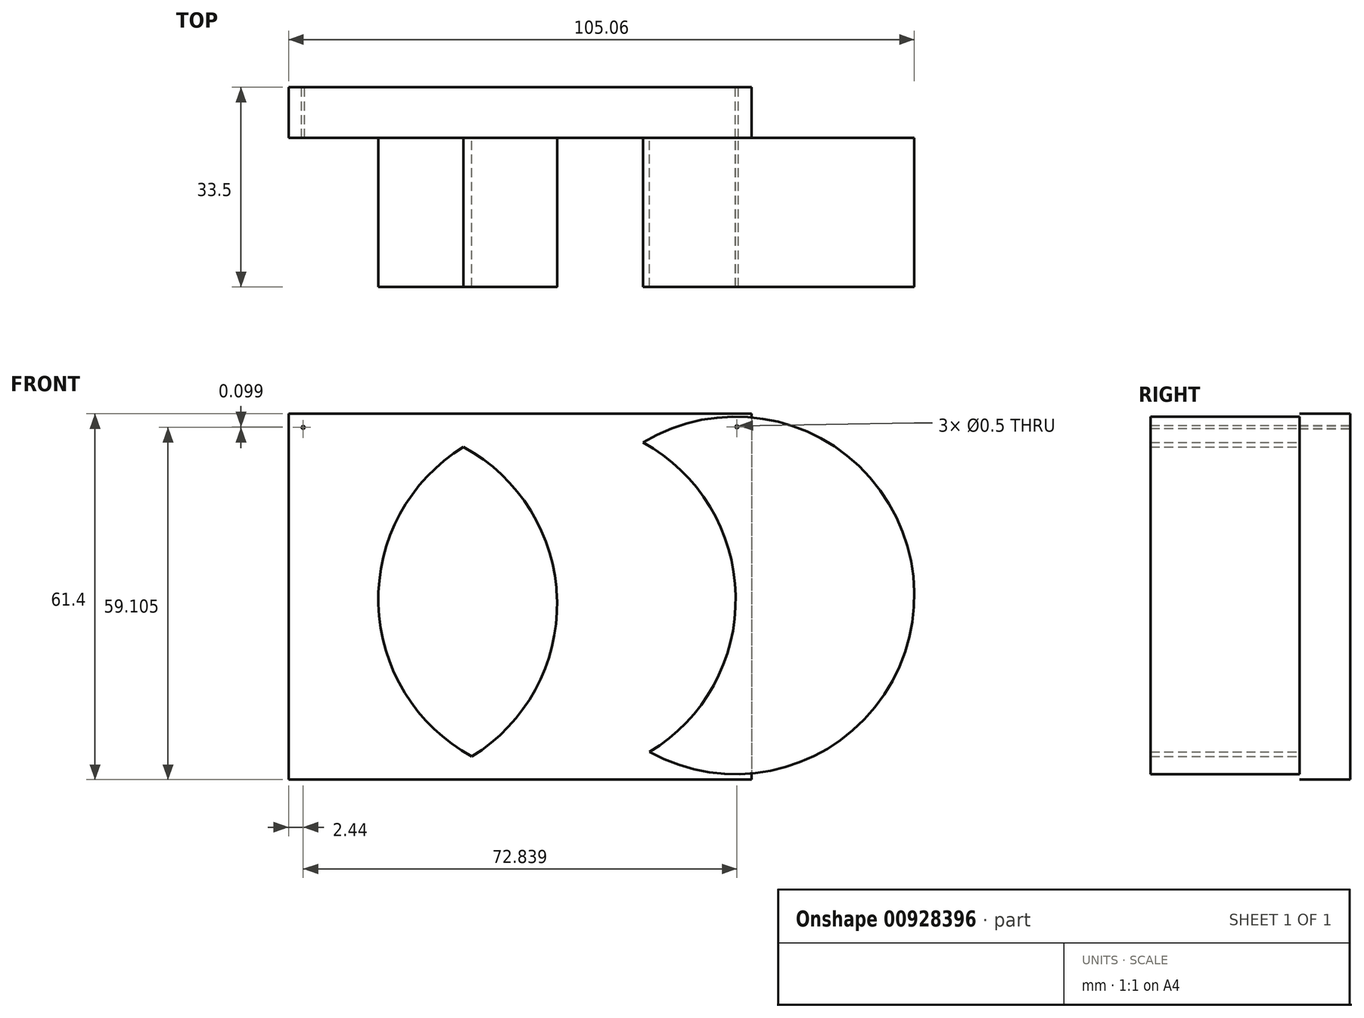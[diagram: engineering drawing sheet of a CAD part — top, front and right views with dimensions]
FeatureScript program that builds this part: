
annotation { "Feature Type Name" : "Feature", "Feature Type Description" : "" }
export const myFeature = defineFeature(function(context is Context, id is Id, definition is map)
    precondition{}
    {
        {
            var Q0;
            Q0=qCreatedBy(makeId("Front.planeOp"),FACE);
            var sketch = newSketch(context, id + "F0", { "sketchPlane" : qUnion([Q0])});
            skCircle(sketch, "E0", {"center": v(-38.91, 38.4) * mm, "radius": 30 * mm});
            skCircle(sketch, "E1", {"center": v(-8.92, 39.21) * mm, "radius": 30 * mm});
            skCircle(sketch, "E2", {"center": v(21.07, 39.84) * mm, "radius": 30 * mm});
            skSolve(sketch);
        }
        {
            var Q0;
            {var subQ0=sQuery(id+"F0.wireOp",EDGE,"E1");var subQ1=sQuery(id+"F0.wireOp",EDGE,"E0");var subQ2=makeQuery(id+"F0.imprint","INTERSECT",VERTEX,{"disambiguationData":[OD(0.0)],"derivedFrom":[subQ1,subQ0]});Q0=makeQuery(id+"F0.imprint","IMPRINT",FACE,{"disambiguationData":[TD([[makeQuery(id+"F0.imprint","IMPRINT",EDGE,{"disambiguationData":[TD([[subQ2,-1.0]])],"derivedFrom":subQ1}),1.0]])]});}
            var Q1;
            {var subQ0=sQuery(id+"F0.wireOp",EDGE,"E2");var subQ1=sQuery(id+"F0.wireOp",EDGE,"E1");var subQ2=makeQuery(id+"F0.imprint","INTERSECT",VERTEX,{"disambiguationData":[OD(0.0)],"derivedFrom":[subQ1,subQ0]});Q1=makeQuery(id+"F0.imprint","IMPRINT",FACE,{"disambiguationData":[TD([[makeQuery(id+"F0.imprint","IMPRINT",EDGE,{"disambiguationData":[TD([[subQ2,1.0]])],"derivedFrom":subQ1}),-1.0]])]});}
            var Q2;
            {var subQ0=sQuery(id+"F0.wireOp",EDGE,"E1");var subQ1=sQuery(id+"F0.wireOp",EDGE,"E0");var subQ2=makeQuery(id+"F0.imprint","INTERSECT",VERTEX,{"disambiguationData":[OD(0.0)],"derivedFrom":[subQ1,subQ0]});Q2=makeQuery(id+"F0.imprint","IMPRINT",FACE,{"disambiguationData":[TD([[makeQuery(id+"F0.imprint","IMPRINT",EDGE,{"disambiguationData":[TD([[subQ2,1.0]])],"derivedFrom":subQ1}),-1.0]])]});}
            var Q3;
            {var subQ0=sQuery(id+"F0.wireOp",EDGE,"E1");var subQ1=sQuery(id+"F0.wireOp",EDGE,"E0");var subQ2=makeQuery(id+"F0.imprint","INTERSECT",VERTEX,{"disambiguationData":[OD(1.0)],"derivedFrom":[subQ1,subQ0]});Q3=makeQuery(id+"F0.imprint","IMPRINT",FACE,{"disambiguationData":[TD([[makeQuery(id+"F0.imprint","IMPRINT",EDGE,{"disambiguationData":[TD([[subQ2,-1.0]])],"derivedFrom":subQ1}),-1.0]])]});}
            extrude(context, id + "F1", {"entities" : qUnion([Q0, Q1, Q2, Q3]), "depth" : 25 * mm, "offsetDistance" : 25 * mm});
        }
        {
            var Q0;
            Q0=qCreatedBy(makeId("Front.planeOp"),FACE);
            var sketch = newSketch(context, id + "F2", { "sketchPlane" : qUnion([Q0])});
            skLineSegment(sketch, "E3.bottom", {"start": v(23.78, 70.34) * mm, "end": v(-54, 70.34) * mm});
            skLineSegment(sketch, "E3.top", {"start": v(23.78, 8.94) * mm, "end": v(-54, 8.94) * mm});
            skLineSegment(sketch, "E3.left", {"start": v(23.78, 70.34) * mm, "end": v(23.78, 8.94) * mm});
            skLineSegment(sketch, "E3.right", {"start": v(-54, 70.34) * mm, "end": v(-54, 8.94) * mm});
            skSolve(sketch);
        }
        {
            var Q0;
            Q0=makeQuery(id+"F2.imprint","IMPRINT",FACE,{"disambiguationData":[TD([[makeQuery(id+"F2.imprint","IMPRINT",EDGE,{"derivedFrom":sQuery(id+"F2.wireOp",EDGE,"E3.bottom")}),1.0]])]});
            extrude(context, id + "F3", {"entities" : qUnion([Q0]), "oppositeDirection" : true, "depth" : 8.5 * mm, "offsetDistance" : 25 * mm});
        }
        {
            var Q0;
            Q0=makeQuery(id+"F3.opExtrude","CAP_FACE",FACE,{"disambiguationData":[OSD([sQuery(id+"F2.wireOp",EDGE,"E3.bottom"),sQuery(id+"F2.wireOp",EDGE,"E3.top"),sQuery(id+"F2.wireOp",EDGE,"E3.left"),sQuery(id+"F2.wireOp",EDGE,"E3.right")])],"isStart":false});
            var sketch = newSketch(context, id + "F4", { "sketchPlane" : qUnion([Q0])});
            skCircle(sketch, "E4", {"center": v(-21.29, 68.14) * mm, "radius": 0.25 * mm});
            skCircle(sketch, "E5", {"center": v(51.55, 68.04) * mm, "radius": 0.25 * mm});
            skSolve(sketch);
        }
        {
            var Q0;
            Q0 = qSketchRegion(id + "F4", true);
            extrude(context, id + "F5", {"entities" : qUnion([Q0]), "operationType" : NewBodyOperationType.REMOVE, "oppositeDirection" : true, "depth" : 52.9 * mm, "offsetDistance" : 25 * mm});
        }
    });
